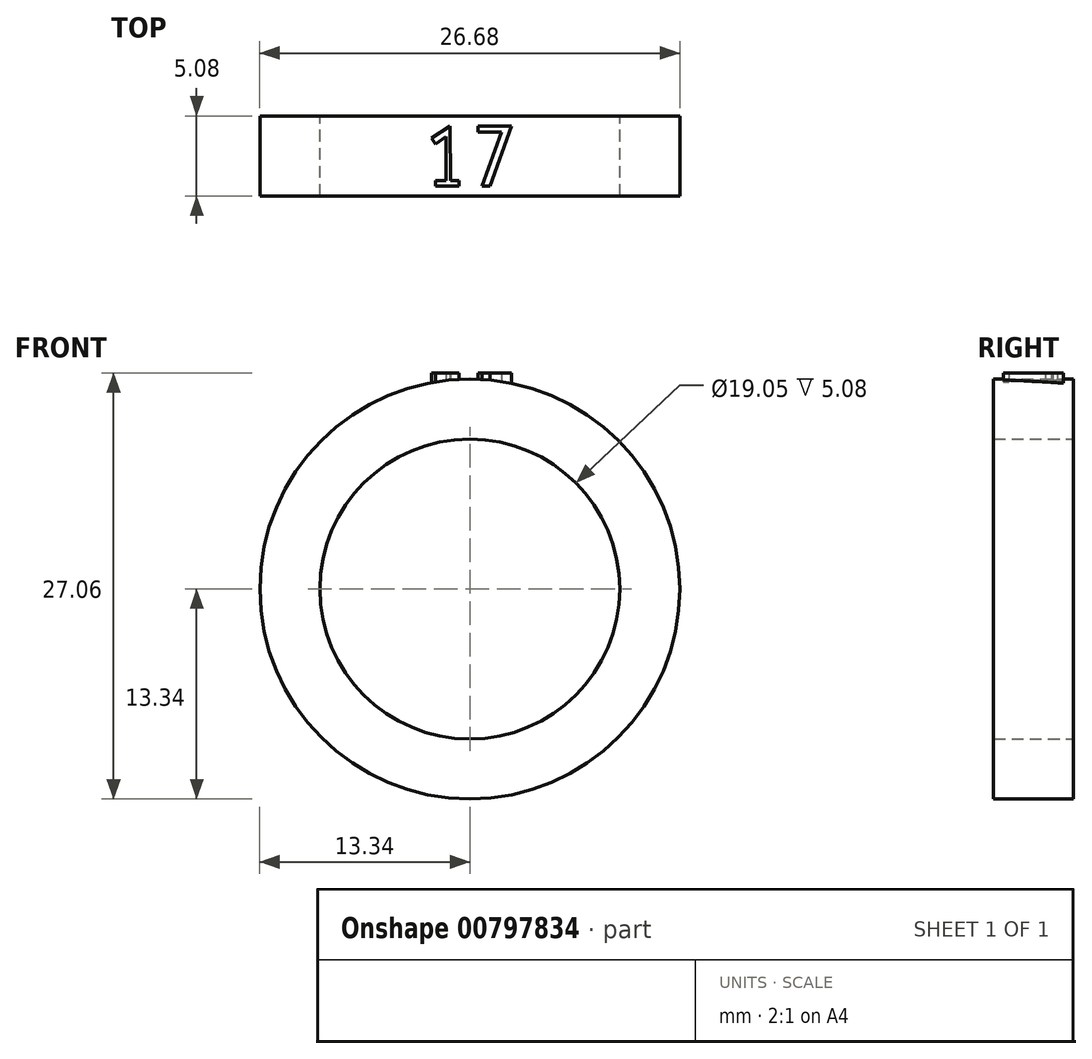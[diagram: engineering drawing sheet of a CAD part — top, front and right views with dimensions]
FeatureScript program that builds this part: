
annotation { "Feature Type Name" : "Feature", "Feature Type Description" : "" }
export const myFeature = defineFeature(function(context is Context, id is Id, definition is map)
    precondition{}
    {
        {
            var Q0;
            Q0=qCreatedBy(makeId("Front.planeOp"),FACE);
            var sketch = newSketch(context, id + "F0", { "sketchPlane" : qUnion([Q0])});
            skCircle(sketch, "E0", {"center": v(0, 0) * mm, "radius": 9.53 * mm});
            skCircle(sketch, "E1", {"center": v(0, 0) * mm, "radius": 13.34 * mm});
            skSolve(sketch);
        }
        {
            var Q0;
            Q0=makeQuery(id+"F0.imprint","IMPRINT",FACE,{"disambiguationData":[TD([[makeQuery(id+"F0.imprint","IMPRINT",EDGE,{"derivedFrom":sQuery(id+"F0.wireOp",EDGE,"E0")}),-1.0]])]});
            extrude(context, id + "F1", {"entities" : qUnion([Q0]), "depth" : 5.08 * mm, "offsetDistance" : 25.4 * mm});
        }
        {
            var Q0;
            Q0=qCreatedBy(makeId("Top.planeOp"),FACE);
            cPlane(context, id + "F2", {"entities" : qUnion([Q0]), "cplaneType" : CPlaneType.OFFSET, "offset" : 10.16 * mm, "width" : 152.4 * mm, "height" : 152.4 * mm});
        }
        {
            var Q0;
            Q0=qCreatedBy(id+"F2.planeOp",FACE);
            var sketch = newSketch(context, id + "F3", { "sketchPlane" : qUnion([Q0])});
            skPoint(sketch, "E2.start.orphan", {"position": v(-5.07, 0) * mm});
            skLineSegment(sketch, "E3", {"start": v(-1.27, -0.64) * mm, "end": v(-2.42, -1.42) * mm});
            skLineSegment(sketch, "E4", {"start": v(-2.42, -1.42) * mm, "end": v(-2.17, -1.78) * mm});
            skLineSegment(sketch, "E5", {"start": v(-2.17, -1.78) * mm, "end": v(-1.51, -1.32) * mm});
            skLineSegment(sketch, "E6", {"start": v(-1.51, -1.32) * mm, "end": v(-1.51, -4.11) * mm});
            skLineSegment(sketch, "E7", {"start": v(-1.51, -4.11) * mm, "end": v(-2.18, -4.11) * mm});
            skLineSegment(sketch, "E8", {"start": v(-2.18, -4.11) * mm, "end": v(-2.18, -4.45) * mm});
            skLineSegment(sketch, "E9", {"start": v(-2.18, -4.45) * mm, "end": v(-0.69, -4.45) * mm});
            skLineSegment(sketch, "E10", {"start": v(-0.69, -4.45) * mm, "end": v(-0.69, -4.11) * mm});
            skLineSegment(sketch, "E11", {"start": v(-0.69, -4.11) * mm, "end": v(-1.23, -4.11) * mm});
            skLineSegment(sketch, "E12", {"start": v(-1.23, -4.11) * mm, "end": v(-1.27, -0.63) * mm});
            skLineSegment(sketch, "E13", {"start": v(0.76, -4.45) * mm, "end": v(2, -1.03) * mm});
            skLineSegment(sketch, "E14", {"start": v(2, -1.03) * mm, "end": v(0.51, -1.03) * mm});
            skLineSegment(sketch, "E15", {"start": v(0.51, -1.03) * mm, "end": v(0.51, -0.63) * mm});
            skLineSegment(sketch, "E16", {"start": v(0.51, -0.64) * mm, "end": v(2.66, -0.64) * mm});
            skLineSegment(sketch, "E17", {"start": v(2.66, -0.63) * mm, "end": v(1.27, -4.45) * mm});
            skLineSegment(sketch, "E18", {"start": v(0.76, -4.45) * mm, "end": v(1.27, -4.45) * mm});
            skPoint(sketch, "E19.start.orphan", {"position": v(-1.27, 0) * mm});
            skPoint(sketch, "E20.orphan", {"position": v(-2.54, 0) * mm});
            skPoint(sketch, "E21.orphan", {"position": v(0, 0) * mm});
            skPoint(sketch, "E22.end.orphan", {"position": v(2.54, 0) * mm});
            skPoint(sketch, "E23.end.orphan", {"position": v(1.27, -0.64) * mm});
            skPoint(sketch, "E23.start.orphan", {"position": v(1.27, 0) * mm});
            skPoint(sketch, "E24.start.orphan", {"position": v(1.27, -5.08) * mm});
            skPoint(sketch, "E25.end.orphan", {"position": v(-1.27, -5.08) * mm});
            skPoint(sketch, "E25.start.orphan", {"position": v(-1.27, -4.45) * mm});
            skSolve(sketch);
        }
        {
            var Q0;
            Q0 = qSketchRegion(id + "F3", true);
            extrude(context, id + "F4", {"entities" : qUnion([Q0]), "operationType" : NewBodyOperationType.ADD, "depth" : 3.56 * mm, "offsetDistance" : 25.4 * mm});
        }
    });
